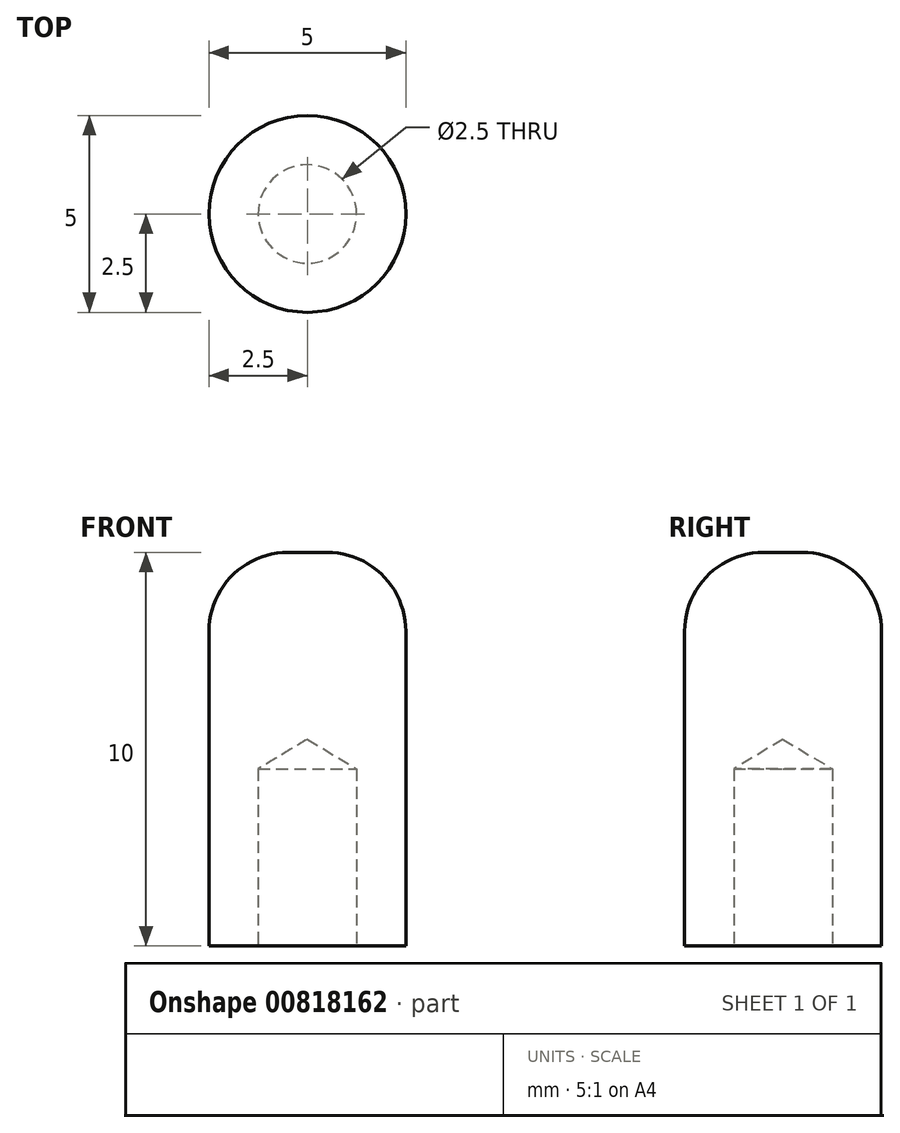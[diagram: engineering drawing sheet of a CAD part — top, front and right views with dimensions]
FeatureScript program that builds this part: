
annotation { "Feature Type Name" : "Feature", "Feature Type Description" : "" }
export const myFeature = defineFeature(function(context is Context, id is Id, definition is map)
    precondition{}
    {
        {
            var Q0;
            Q0=qCreatedBy(makeId("Top.planeOp"),FACE);
            var sketch = newSketch(context, id + "F0", { "sketchPlane" : qUnion([Q0])});
            skCircle(sketch, "E0", {"center": v(0, 0) * mm, "radius": 1.25 * mm});
            skCircle(sketch, "E1", {"center": v(0, 0) * mm, "radius": 2.5 * mm});
            skSolve(sketch);
        }
        {
            var Q0;
            Q0 = qSketchRegion(id + "F0", true);
            var Q1;
            Q1=makeQuery(id+"F0.imprint","IMPRINT",FACE,{"disambiguationData":[TD([[makeQuery(id+"F0.imprint","IMPRINT",EDGE,{"derivedFrom":sQuery(id+"F0.wireOp",EDGE,"E0")}),1.0]])]});
            extrude(context, id + "F1", {"entities" : qUnion([Q0, Q1]), "depth" : 10 * mm, "offsetDistance" : 25 * mm});
        }
        {
            var Q0;
            Q0=makeQuery(id+"F1.opExtrude","CAP_EDGE",EDGE,{"disambiguationData":[OSD([sQuery(id+"F0.wireOp",EDGE,"E1")])],"isStart":false});
            fillet(context, id + "F2", {"entities" : qUnion([Q0]), "radius" : 2 * mm, "tangentPropagation" : true, "allowEdgeOverflow" : false});
        }
        {
            var Q0;
            Q0=makeQuery(id+"F1.opExtrude","CAP_FACE",FACE,{"disambiguationData":[OSD([sQuery(id+"F0.wireOp",EDGE,"E1")])],"isStart":true});
            var sketch = newSketch(context, id + "F3", { "sketchPlane" : qUnion([Q0])});
            skPoint(sketch, "E2", {"position": v(0, 0) * mm});
            skSolve(sketch);
        }
        {
            var Q0;
            Q0=sQuery(id+"F3.wireOp",VERTEX,"E2");
            var Q1;
            Q1=makeQuery(id+"F1.opExtrude","SWEPT_BODY",BODY,{"disambiguationData":[OSD([sQuery(id+"F0.wireOp",EDGE,"E1")])]});
            hole(context, id + "F4", {"style" : HoleStyle.SIMPLE, "endStyle" : HoleEndStyle.BLIND, "holeDiameter" : 2.5 * mm, "majorDiameter" : 5 * mm, "holeDepth" : 4.5 * mm, "isTappedThrough" : true, "tappedDepth" : 12 * mm, "tapClearance" : 3, "startFromSketch" : true, "locations" : qUnion([Q0]), "scope" : qUnion([Q1])});
        }
    });
